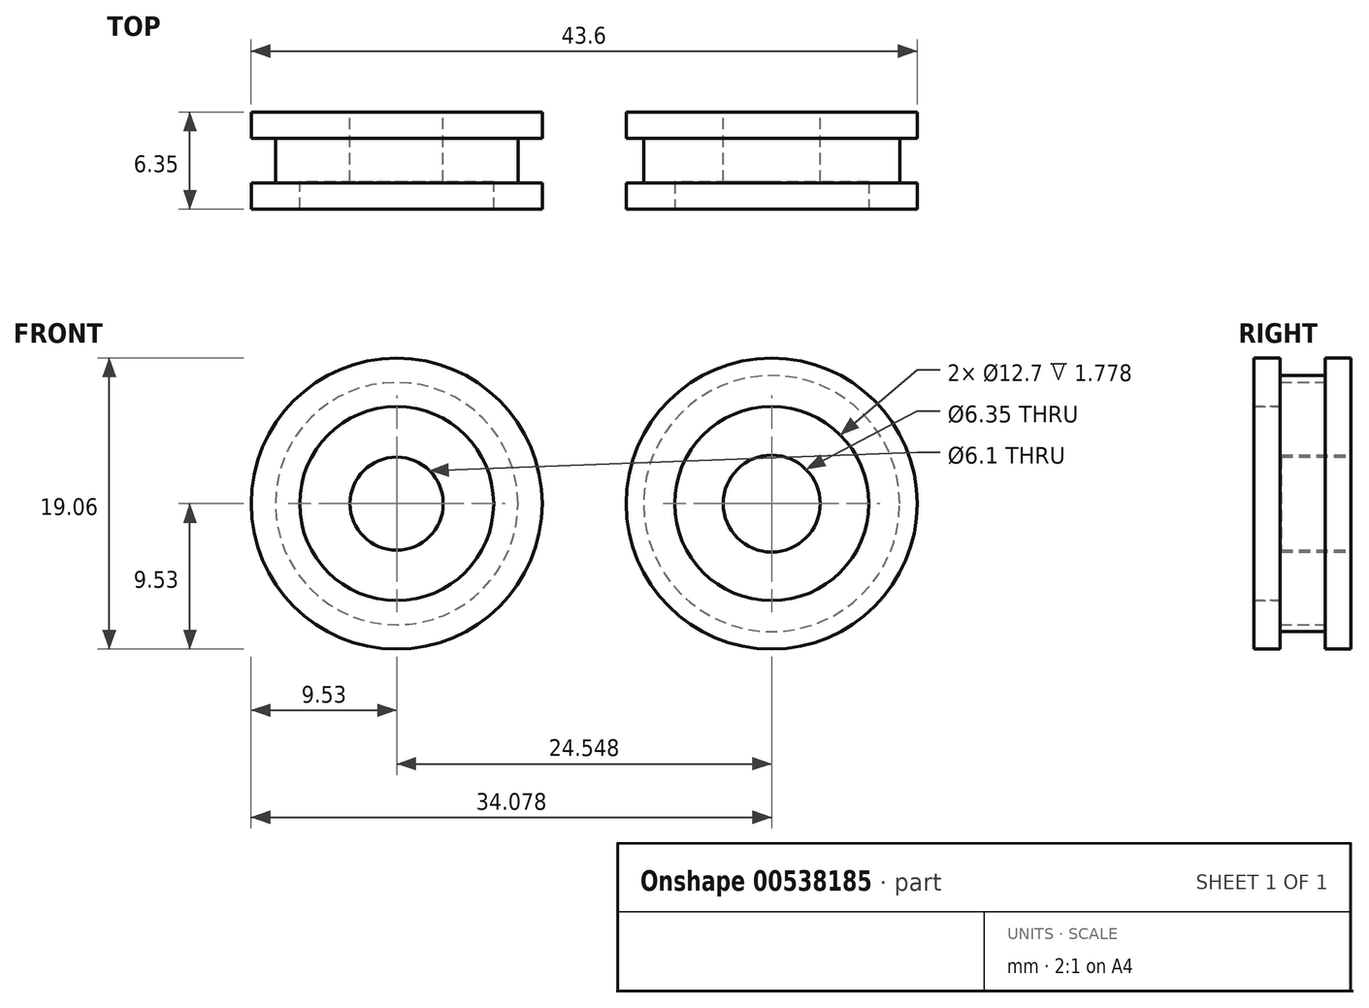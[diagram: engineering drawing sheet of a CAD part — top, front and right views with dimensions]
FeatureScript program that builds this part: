
annotation { "Feature Type Name" : "Feature", "Feature Type Description" : "" }
export const myFeature = defineFeature(function(context is Context, id is Id, definition is map)
    precondition{}
    {
        {
            var Q0;
            Q0=qCreatedBy(makeId("Top.planeOp"),FACE);
            var sketch = newSketch(context, id + "F0", { "sketchPlane" : qUnion([Q0])});
            skLineSegment(sketch, "E0.bottom", {"start": v(3.05, 0) * mm, "end": v(9.53, 0) * mm});
            skLineSegment(sketch, "E0.top", {"start": v(6.35, -6.35) * mm, "end": v(9.53, -6.35) * mm});
            skLineSegment(sketch, "E0.left", {"start": v(3.05, 0) * mm, "end": v(3.05, -4.57) * mm});
            skLineSegment(sketch, "E1.top", {"start": v(6.35, -4.57) * mm, "end": v(3.05, -4.57) * mm});
            skLineSegment(sketch, "E1.left", {"start": v(6.35, -6.35) * mm, "end": v(6.35, -4.57) * mm});
            skLineSegment(sketch, "E2", {"start": v(0, 0) * mm, "end": v(0, -6.35) * mm, "construction": true});
            skLineSegment(sketch, "E3", {"start": v(9.53, 0) * mm, "end": v(9.53, -1.7) * mm});
            skLineSegment(sketch, "E4", {"start": v(9.53, -1.7) * mm, "end": v(7.94, -1.7) * mm});
            skLineSegment(sketch, "E5", {"start": v(7.94, -1.7) * mm, "end": v(7.94, -4.65) * mm});
            skLineSegment(sketch, "E6", {"start": v(7.94, -4.65) * mm, "end": v(9.53, -4.65) * mm});
            skLineSegment(sketch, "E7", {"start": v(9.53, -4.65) * mm, "end": v(9.53, -6.35) * mm});
            skLineSegment(sketch, "E8", {"start": v(7.94, -3.17) * mm, "end": v(0, -3.18) * mm, "construction": true});
            skSolve(sketch);
        }
        {
            var Q0;
            Q0 = qSketchRegion(id + "F0", true);
            var Q1;
            Q1=sQuery(id+"F0.wireOp",EDGE,"E2");
            revolve(context, id + "F1", {"entities" : qUnion([Q0]), "axis" : qUnion([Q1]), "revolveType" : RevolveType.FULL});
        }
        {
            var Q0;
            Q0=qCreatedBy(makeId("Front.planeOp"),FACE);
            var sketch = newSketch(context, id + "F2", { "sketchPlane" : qUnion([Q0])});
            skCircle(sketch, "E9", {"center": v(24.55, 0) * mm, "radius": 9.53 * mm});
            skSolve(sketch);
        }
        {
            var Q0;
            Q0 = qSketchRegion(id + "F2", true);
            extrude(context, id + "F3", {"entities" : qUnion([Q0]), "depth" : 6.35 * mm, "offsetDistance" : 25.4 * mm});
        }
        {
            var Q0;
            Q0=makeQuery(id+"F3.opExtrude","CAP_FACE",FACE,{"disambiguationData":[OSD([sQuery(id+"F2.wireOp",EDGE,"E9")])],"isStart":true});
            var Q1;
            Q1=makeQuery(id+"F3.opExtrude","CAP_FACE",FACE,{"disambiguationData":[OSD([sQuery(id+"F2.wireOp",EDGE,"E9")])],"isStart":false});
            cPlane(context, id + "F4", {"entities" : qUnion([Q0, Q1]), "cplaneType" : CPlaneType.MID_PLANE, "offset" : 25.4 * mm, "width" : 152.4 * mm, "height" : 152.4 * mm});
        }
        {
            var Q0;
            Q0=qCreatedBy(id+"F4.planeOp",FACE);
            var sketch = newSketch(context, id + "F5", { "sketchPlane" : qUnion([Q0])});
            skCircle(sketch, "E10.0", {"center": v(-24.55, 0) * mm, "radius": 9.53 * mm});
            skCircle(sketch, "E11", {"center": v(-24.55, 0) * mm, "radius": 8.38 * mm});
            skSolve(sketch);
        }
        {
            var Q0;
            Q0 = qSketchRegion(id + "F5", true);
            extrude(context, id + "F6", {"entities" : qUnion([Q0]), "operationType" : NewBodyOperationType.REMOVE, "endBound" : BoundingType.SYMMETRIC, "oppositeDirection" : true, "depth" : 2.95 * mm, "offsetDistance" : 25.4 * mm, "hasSecondDirection" : true, "secondDirectionOppositeDirection" : false, "secondDirectionDepth" : 25.4 * mm});
        }
        {
            var Q0;
            Q0=makeQuery(id+"F3.opExtrude","CAP_FACE",FACE,{"disambiguationData":[OSD([sQuery(id+"F2.wireOp",EDGE,"E9")])],"isStart":true});
            var sketch = newSketch(context, id + "F7", { "sketchPlane" : qUnion([Q0])});
            skCircle(sketch, "E12", {"center": v(-24.55, 0) * mm, "radius": 3.18 * mm});
            skSolve(sketch);
        }
        {
            var Q0;
            Q0 = qSketchRegion(id + "F7", true);
            extrude(context, id + "F8", {"entities" : qUnion([Q0]), "operationType" : NewBodyOperationType.REMOVE, "endBound" : BoundingType.THROUGH_ALL, "oppositeDirection" : true, "depth" : 25.4 * mm, "offsetDistance" : 25.4 * mm});
        }
        {
            var Q0;
            Q0=makeQuery(id+"F3.opExtrude","CAP_FACE",FACE,{"disambiguationData":[OSD([sQuery(id+"F2.wireOp",EDGE,"E9")])],"isStart":false});
            var sketch = newSketch(context, id + "F9", { "sketchPlane" : qUnion([Q0])});
            skCircle(sketch, "E13", {"center": v(24.55, 0) * mm, "radius": 6.35 * mm});
            skSolve(sketch);
        }
        {
            var Q0;
            Q0=makeQuery(id+"F9.imprint","IMPRINT",FACE,{"disambiguationData":[TD([[makeQuery(id+"F9.imprint","IMPRINT",EDGE,{"derivedFrom":makeQuery(id+"F8.boolean.opBoolean","INTERSECT",EDGE,{"derivedFrom":[makeQuery(id+"F3.opExtrude","CAP_FACE",FACE,{"disambiguationData":[OSD([sQuery(id+"F2.wireOp",EDGE,"E9")])],"isStart":false}),makeQuery(id+"F8.opExtrude","SWEPT_FACE",FACE,{"disambiguationData":[OSD([sQuery(id+"F7.wireOp",EDGE,"E12")])]})]})}),1.0]])]});
            var Q1;
            Q1=makeQuery(id+"F9.imprint","IMPRINT",FACE,{"disambiguationData":[TD([[makeQuery(id+"F9.imprint","IMPRINT",EDGE,{"derivedFrom":sQuery(id+"F9.wireOp",EDGE,"E13")}),1.0]])]});
            extrude(context, id + "F10", {"entities" : qUnion([Q0, Q1]), "operationType" : NewBodyOperationType.REMOVE, "oppositeDirection" : true, "depth" : 1.78 * mm, "offsetDistance" : 25.4 * mm});
        }
    });
